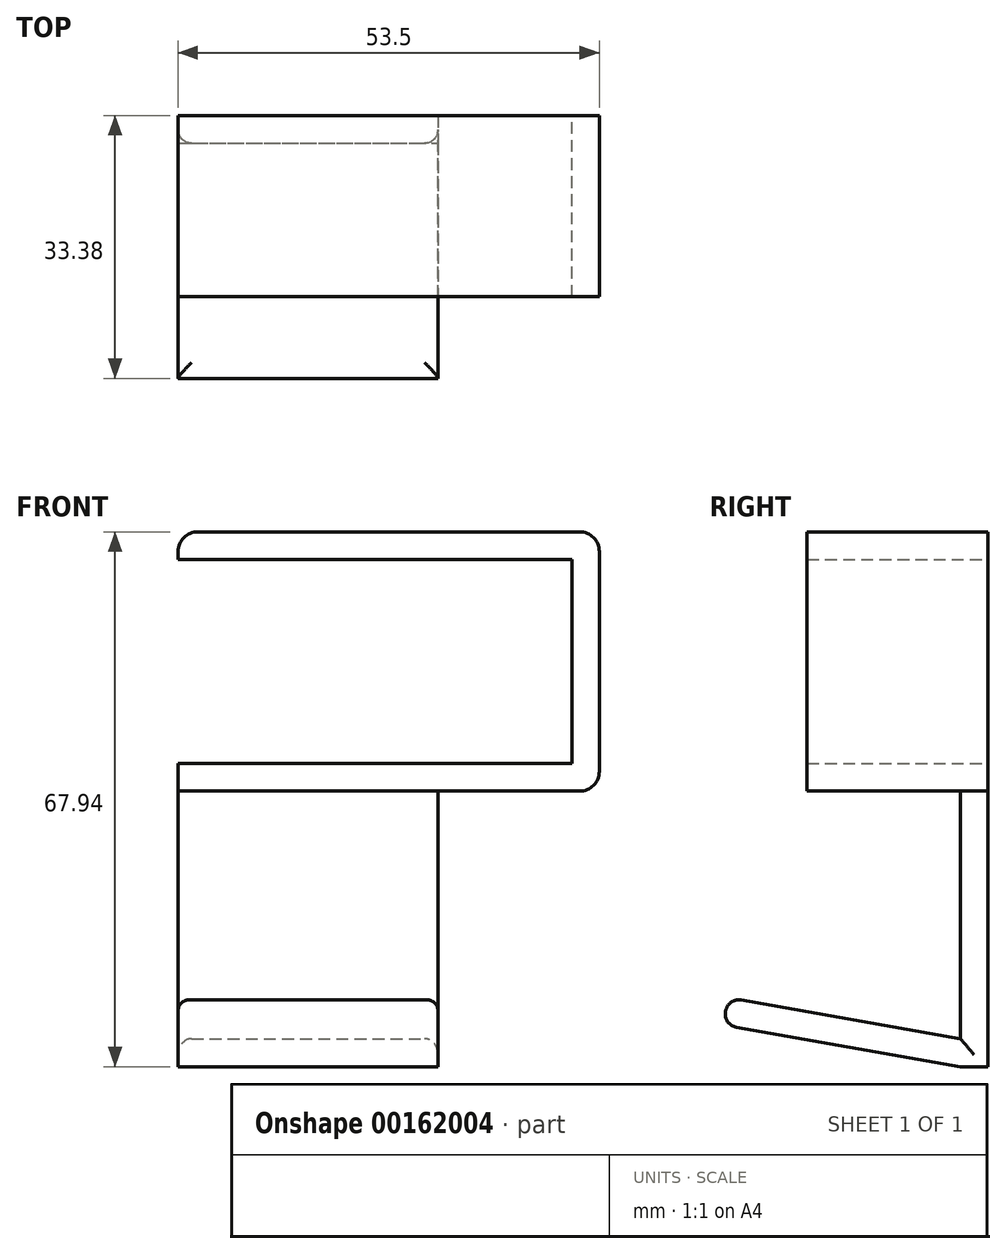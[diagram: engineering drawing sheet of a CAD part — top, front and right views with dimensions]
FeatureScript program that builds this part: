
annotation { "Feature Type Name" : "Feature", "Feature Type Description" : "" }
export const myFeature = defineFeature(function(context is Context, id is Id, definition is map)
    precondition{}
    {
        {
            var Q0;
            Q0=qCreatedBy(makeId("Front.planeOp"),FACE);
            var sketch = newSketch(context, id + "F0", { "sketchPlane" : qUnion([Q0])});
            skLineSegment(sketch, "E0", {"start": v(-53.5, 29.44) * mm, "end": v(-3.5, 29.44) * mm});
            skLineSegment(sketch, "E1", {"start": v(-3.5, 29.44) * mm, "end": v(-3.5, 3.5) * mm});
            skLineSegment(sketch, "E2", {"start": v(-3.5, 3.5) * mm, "end": v(-53.5, 3.5) * mm});
            skLineSegment(sketch, "E3.0", {"start": v(0, 0) * mm, "end": v(-53.5, 0) * mm});
            skLineSegment(sketch, "E3.1", {"start": v(0, 32.94) * mm, "end": v(0, 0) * mm});
            skLineSegment(sketch, "E3.2", {"start": v(-53.5, 32.94) * mm, "end": v(0, 32.94) * mm});
            skLineSegment(sketch, "E4", {"start": v(-53.5, 32.94) * mm, "end": v(-53.5, 29.44) * mm});
            skLineSegment(sketch, "E5", {"start": v(-53.5, 3.5) * mm, "end": v(-53.5, 0) * mm});
            skSolve(sketch);
        }
        {
            var Q0;
            Q0=makeQuery(id+"F0.imprint","IMPRINT",FACE,{"disambiguationData":[TD([[makeQuery(id+"F0.imprint","IMPRINT",EDGE,{"derivedFrom":sQuery(id+"F0.wireOp",EDGE,"E0")}),1.0]])]});
            extrude(context, id + "F1", {"entities" : qUnion([Q0]), "depth" : 23 * mm});
        }
        {
            var Q0;
            Q0=makeQuery(id+"F1.opExtrude","SWEPT_FACE",FACE,{"disambiguationData":[OSD([sQuery(id+"F0.wireOp",EDGE,"E3.0")])]});
            var sketch = newSketch(context, id + "F2", { "sketchPlane" : qUnion([Q0])});
            skLineSegment(sketch, "E6.bottom", {"start": v(-53.5, 0) * mm, "end": v(-20.5, 0) * mm});
            skLineSegment(sketch, "E6.top", {"start": v(-53.5, 3.5) * mm, "end": v(-20.5, 3.5) * mm});
            skLineSegment(sketch, "E6.left", {"start": v(-53.5, 0) * mm, "end": v(-53.5, 3.5) * mm});
            skLineSegment(sketch, "E6.right", {"start": v(-20.5, 0) * mm, "end": v(-20.5, 3.5) * mm});
            skSolve(sketch);
        }
        {
            var Q0;
            Q0=makeQuery(id+"F2.imprint","IMPRINT",FACE,{"disambiguationData":[TD([[makeQuery(id+"F2.imprint","IMPRINT",EDGE,{"derivedFrom":sQuery(id+"F2.wireOp",EDGE,"E6.bottom")}),-1.0]])]});
            extrude(context, id + "F3", {"entities" : qUnion([Q0]), "operationType" : NewBodyOperationType.ADD, "depth" : 35 * mm});
        }
        {
            var Q0;
            Q0=makeQuery(id+"F3.opExtrude","SWEPT_FACE",FACE,{"disambiguationData":[OSD([sQuery(id+"F2.wireOp",EDGE,"E6.right")])]});
            var sketch = newSketch(context, id + "F4", { "sketchPlane" : qUnion([Q0])});
            skLineSegment(sketch, "E7", {"start": v(-3.5, -35) * mm, "end": v(-33.65, -29.68) * mm});
            skLineSegment(sketch, "E8", {"start": v(-33.65, -29.68) * mm, "end": v(-33.04, -26.24) * mm});
            skLineSegment(sketch, "E9", {"start": v(-33.04, -26.24) * mm, "end": v(-3.5, -31.45) * mm});
            skSolve(sketch);
        }
        {
            var Q0;
            {var subQ0=sQuery(id+"F4.wireOp",EDGE,"E7");Q0=makeQuery(id+"F4.imprint","IMPRINT",FACE,{"disambiguationData":[TD([[makeQuery(id+"F4.imprint","IMPRINT",EDGE,{"derivedFrom":subQ0}),-1.0]])]});}
            var Q1;
            Q1=makeQuery(id+"F3.boolean.opBoolean","MERGE",FACE,{"derivedFrom":[makeQuery(id+"F1.opExtrude","SWEPT_FACE",FACE,{"disambiguationData":[OSD([sQuery(id+"F0.wireOp",EDGE,"E5")])]}),makeQuery(id+"F3.opExtrude","SWEPT_FACE",FACE,{"disambiguationData":[OSD([sQuery(id+"F2.wireOp",EDGE,"E6.left")])]})]});
            extrude(context, id + "F5", {"entities" : qUnion([Q0]), "operationType" : NewBodyOperationType.ADD, "endBound" : BoundingType.UP_TO_SURFACE, "oppositeDirection" : true, "endBoundEntityFace" : qUnion([Q1]), "depth" : 25 * mm});
        }
        {
            var Q0;
            Q0=makeQuery(id+"F1.opExtrude","SWEPT_EDGE",EDGE,{"disambiguationData":[OSD([sQuery(id+"F0.wireOp",EDGE,"E3.2"),sQuery(id+"F0.wireOp",EDGE,"E4")])]});
            var Q1;
            Q1=makeQuery(id+"F1.opExtrude","SWEPT_EDGE",EDGE,{"disambiguationData":[OSD([sQuery(id+"F0.wireOp",EDGE,"E3.1"),sQuery(id+"F0.wireOp",EDGE,"E3.2")])]});
            var Q2;
            Q2=makeQuery(id+"F1.opExtrude","SWEPT_EDGE",EDGE,{"disambiguationData":[OSD([sQuery(id+"F0.wireOp",EDGE,"E3.0"),sQuery(id+"F0.wireOp",EDGE,"E3.1")])]});
            fillet(context, id + "F6", {"entities" : qUnion([Q0, Q1, Q2]), "radius" : 2.5 * mm, "tangentPropagation" : true, "allowEdgeOverflow" : false});
        }
        {
            var Q0;
            Q0=makeQuery(id+"F5.opExtrude","SWEPT_EDGE",EDGE,{"disambiguationData":[OSD([sQuery(id+"F4.wireOp",EDGE,"E7"),sQuery(id+"F4.wireOp",EDGE,"E8")])]});
            var Q1;
            Q1=makeQuery(id+"F5.opExtrude","SWEPT_EDGE",EDGE,{"disambiguationData":[OSD([sQuery(id+"F4.wireOp",EDGE,"E8"),sQuery(id+"F4.wireOp",EDGE,"E9")])]});
            var Q2;
            Q2=makeQuery(id+"F5.opExtrude","CAP_EDGE",EDGE,{"disambiguationData":[OSD([sQuery(id+"F4.wireOp",EDGE,"E9")])],"isStart":true});
            var Q3;
            Q3=makeQuery(id+"F5.opExtrude","CAP_EDGE",EDGE,{"disambiguationData":[OSD([sQuery(id+"F4.wireOp",EDGE,"E9")])],"isStart":false});
            var Q4;
            Q4=makeQuery(id+"F3.opExtrude","SWEPT_EDGE",EDGE,{"disambiguationData":[OSD([sQuery(id+"F0.wireOp",EDGE,"E3.0"),sQuery(id+"F0.wireOp",EDGE,"E5"),sQuery(id+"F2.wireOp",EDGE,"E6.top"),sQuery(id+"F2.wireOp",EDGE,"E6.left")])]});
            var Q5;
            Q5=makeQuery(id+"F3.opExtrude","SWEPT_EDGE",EDGE,{"disambiguationData":[OSD([sQuery(id+"F2.wireOp",EDGE,"E6.top"),sQuery(id+"F2.wireOp",EDGE,"E6.right")])]});
            var Q6;
            Q6=makeQuery(id+"F3.opExtrude","CAP_EDGE",EDGE,{"disambiguationData":[OSD([sQuery(id+"F2.wireOp",EDGE,"E6.top")])],"isStart":true});
            fillet(context, id + "F7", {"entities" : qUnion([Q0, Q1, Q2, Q3, Q4, Q5, Q6]), "radius" : 1.7 * mm, "tangentPropagation" : true, "allowEdgeOverflow" : false});
        }
    });
